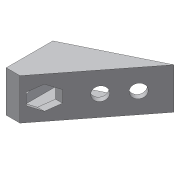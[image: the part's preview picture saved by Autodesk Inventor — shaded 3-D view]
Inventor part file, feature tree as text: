
AUTODESK INVENTOR PART (.ipt)
format: ipt  version: 2013 (Build 170138000, 138)  size: 108,032 bytes
history: native  units: mm
features: hole x3, extrude x2, sketch x2, shell x1
ambient origin geometry x8: Origin, YZ Plane, XZ Plane, XY Plane, X Axis, Y Axis, Z Axis, Center Point
bodies: Volumenkörper1 (feature_tree)
feature tree (8):
  extrude  "Extrusion1"  Depth=15.0mm TaperAngle=0.0deg
  hole  "Bohrung1"  [1 undecoded]
  shell  "Wandstärke3"  Thickness=40.0mm
  extrude  "Extrusion4"  Depth=2.0mm
  hole  "Bohrung6"  [1 undecoded]
  hole  "Bohrung7"  [1 undecoded]
  sketch  "Skizze1"  dims[d0=17.0mm d3=15.0mm d4=0.0mm]
  sketch  "Skizze5"  dims[d6=5.0mm d7=7.5mm d8=5.0mm d9=6.0mm d10=4.0mm d11=2.0mm d12=90.0deg d13=8.0mm d14=20.594885mm d46=5.0mm d48=40.0mm d68=2.0mm d69=10.0mm d70=0.0mm d71=4.3mm d72=5.0mm d73=5.5mm d74=5.0mm d75=6.0mm d76=4.0mm d77=2.0mm d78=90.0deg d79=8.0mm d80=20.594885mm d81=15.0mm d82=5.5mm d83=5.0mm d84=6.0mm d85=4.0mm d86=2.0mm d87=90.0deg d88=8.0mm d89=20.594885mm]
note: 3 required parameter values undecoded (feature->parameter linkage not recoverable at this tier; creation-order binding heuristic only, values carry confidence <= 0.55)
